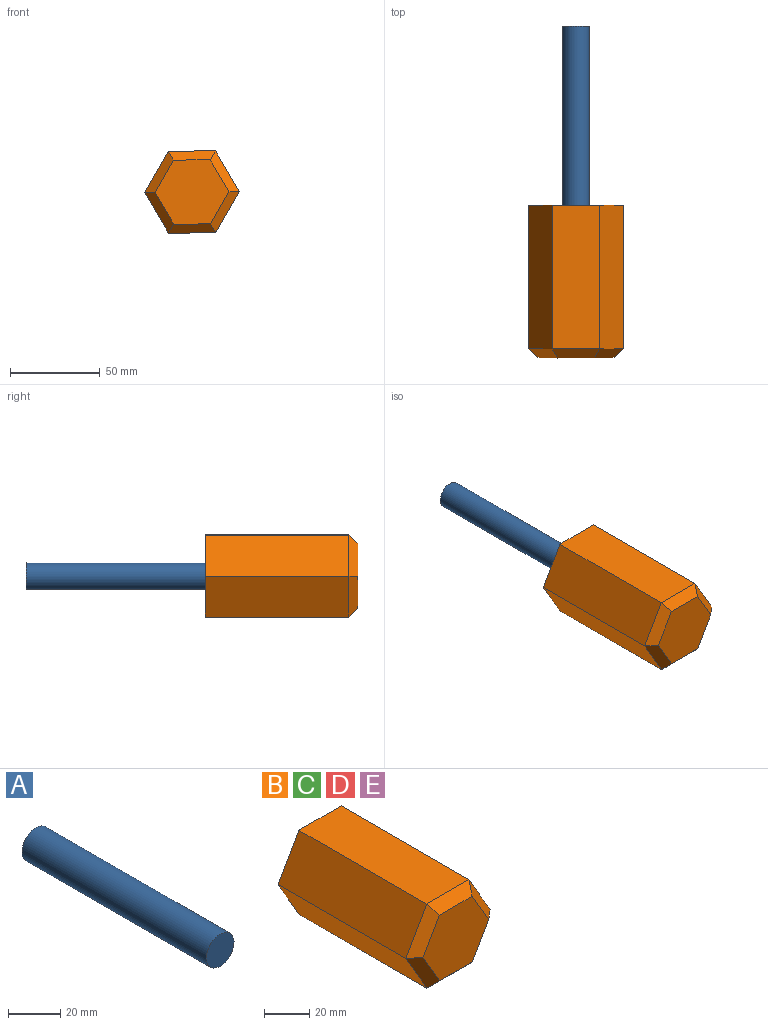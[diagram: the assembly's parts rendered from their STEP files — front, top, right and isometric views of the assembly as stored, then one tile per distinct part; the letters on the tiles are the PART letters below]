
ASSEMBLY  parts=5 mates=1
PART A: 3 faces, bbox 15x100x15 mm
  f0: cylinder r=7.5mm len=100mm, axis (0,1,0), area 4712.4mm2, adj f1,f2
  f1: plane 15x15mm, normal (0,-1,0), area 176.7mm2, adj f0
  f2: plane 15x15mm, normal (0,1,0), area 176.7mm2, adj f0
PART B: 16 faces, bbox 52.8x85x45.8 mm
  f0: plane 80x22.89mm, normal (0.87,0,-0.5), area 2110.6mm2, adj f1,f5,f7,f13
  f1: plane 80x22.8mm, normal (0.86,0,0.5), area 2110.6mm2, adj f0,f2,f7,f12
  f2: plane 80x26.38mm, normal (0,0,1), area 2110.6mm2, adj f1,f3,f7,f10
  f3: plane 80x22.89mm, normal (-0.87,0,0.5), area 2110.6mm2, adj f2,f4,f7,f8
  f4: plane 80x22.8mm, normal (-0.86,0,-0.5), area 2110.6mm2, adj f3,f5,f7,f9
  f5: plane 80x26.38mm, normal (0,0,-1), area 2110.6mm2, adj f0,f4,f7,f11
  f6: plane 41.22x35.77mm, normal (0,-1,0), area 1103.4mm2, adj f8,f9,f10,f11,f12,f13
  f7: plane 52.76x45.79mm, normal (0,1,0), area 1631.6mm2, adj f0,f1,f2,f3,f4,f5,f14
  f8: plane 22.89x16.02mm, normal (-0.61,-0.71,0.35), area 166.1mm2, adj f3,f6,f9,f10
  f9: plane 22.82x16.14mm, normal (-0.61,-0.71,-0.36), area 166.1mm2, adj f4,f6,f8,f11
  f10: plane 26.38x5.08mm, normal (0,-0.71,0.71), area 166.1mm2, adj f2,f6,f8,f12
  f11: plane 26.38x5.08mm, normal (0,-0.71,-0.71), area 166.1mm2, adj f5,f6,f9,f13
  f12: plane 22.82x16.14mm, normal (0.61,-0.71,0.36), area 166.1mm2, adj f1,f6,f10,f13
  f13: plane 22.89x16.02mm, normal (0.61,-0.71,-0.35), area 166.1mm2, adj f0,f6,f11,f12
  f14: cylinder r=7.5mm len=25mm, axis (0,1,0), area 1178.1mm2, adj f7,f15
  f15: plane 15x15mm, normal (0,1,0), area 176.7mm2, adj f14
PART C: same geometry as B
PART D: same geometry as B
PART E: same geometry as B
PLACE A t=(0,100,0)mm
PLACE B at identity
PLACE C at identity
PLACE D at identity
PLACE E at identity
MATE fastened A.f0 <-> D.f14  axis (0,-1,0) through (0,0,0)mm
